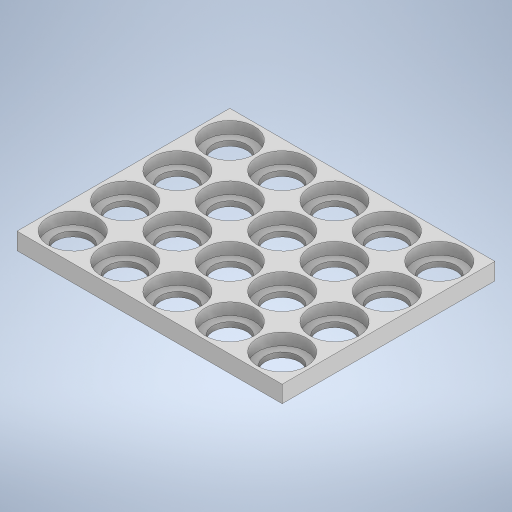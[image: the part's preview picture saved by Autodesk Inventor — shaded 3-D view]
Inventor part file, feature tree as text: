
AUTODESK INVENTOR PART (.ipt)
format: ipt  version: 2023 (Build 270158000, 158)  size: 400,384 bytes
history: native  units: mm
features: extrude x3, sketch x3, other x1
ambient origin geometry x8: Origin, YZ Plane, XZ Plane, XY Plane, X Axis, Y Axis, Z Axis, Center Point
bodies: Body1 (feature_tree)
feature tree (7):
  other  "Sólido1"
  extrude  "Extrusión1"  Depth=63.0mm
  extrude  "Extrusión2"  Depth=5.0mm
  extrude  "Extrusión3"  Depth=3.5mm TaperAngle=0.0deg
  sketch  "Boceto1"  dims[d0=78.5mm d1=63.0mm]
  sketch  "Boceto2"  dims[d2=5.0mm d3=0.0mm d4=14.5mm]
  sketch  "Boceto3"  dims[d6=23.25mm d8=3.5mm d9=0.0mm d10=10.0mm d11=4.0mm d12=0.0mm d13=7.25mm d14=1.0mm d15=7.25mm d16=1.0mm d17=40.0mm d19=15.5mm d20=10.0mm d22=10.0mm d24=1.0mm d25=1.0mm d26=50.0mm d28=15.5mm d29=10.0mm d31=10.0mm d33=1.0mm d34=1.0mm d35=40.0mm d37=15.5mm d38=10.0mm d40=10.0mm d42=50.0mm d44=15.5mm d45=10.0mm d47=10.0mm d49=2.25mm]
